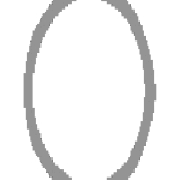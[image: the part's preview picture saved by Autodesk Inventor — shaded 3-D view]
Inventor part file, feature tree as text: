
AUTODESK INVENTOR PART (.ipt)
format: ipt  version: 2021 (Build 250183000, 183)  size: 109,056 bytes
history: native  units: in
note: dims shown in document units (in); Inventor stores cm internally (conversion verified against a paired STEP export)
features: other x4, sketch x3, plane x1
ambient origin geometry x8: Origin, YZ Plane, XZ Plane, XY Plane, X Axis, Y Axis, Z Axis, Center Point
bodies: Solid1 (feature_tree), Body (feature_tree)
feature tree (8):
  other  "Driven Length"
  other  "Frame Generator"
  other  "Start Plane"
  other  "End Plane"
  sketch  "Sketch"  dims[d2=31.6893in d4=-0.0in d5=31.6893in d6=0.12in d7=0.0in d8=90.0deg d9=31.6893in]
  sketch  "Sketch2"  dims[d0=1.0in]
  plane  "Work Plane3"
  sketch  "Sketch3"  dims[d1=0.065in]
